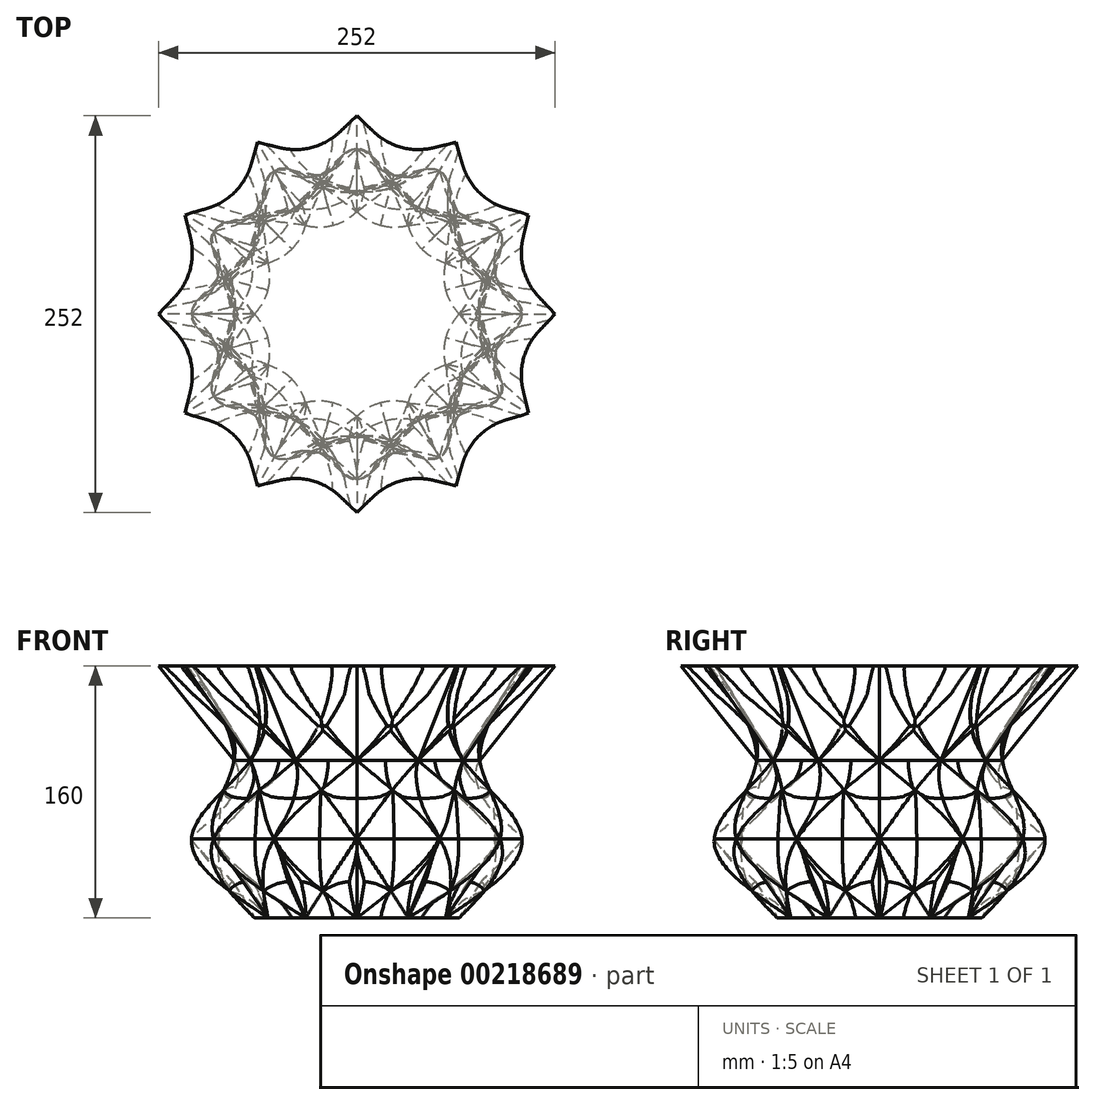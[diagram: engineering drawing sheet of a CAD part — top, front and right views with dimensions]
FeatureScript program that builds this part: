
annotation { "Feature Type Name" : "Feature", "Feature Type Description" : "" }
export const myFeature = defineFeature(function(context is Context, id is Id, definition is map)
    precondition{}
    {
        {
            var Q0;
            Q0=qCreatedBy(makeId("Top.planeOp"),FACE);
            var sketch = newSketch(context, id + "F0", { "sketchPlane" : qUnion([Q0])});
            skCircle(sketch, "E0", {"center": v(0, 0) * mm, "radius": 53.63 * mm, "construction": true});
            skLineSegment(sketch, "E1", {"start": v(-13.88, 51.8) * mm, "end": v(0, 65.07) * mm});
            skLineSegment(sketch, "E2.MirrorCS", {"start": v(13.88, 51.8) * mm, "end": v(0, 65.07) * mm});
            skLineSegment(sketch, "E3.1.0", {"start": v(-37.93, 37.93) * mm, "end": v(-32.54, 56.35) * mm});
            skLineSegment(sketch, "E3.1.1", {"start": v(-13.88, 51.8) * mm, "end": v(-32.54, 56.35) * mm});
            skLineSegment(sketch, "E3.2.0", {"start": v(-51.8, 13.88) * mm, "end": v(-56.35, 32.54) * mm});
            skLineSegment(sketch, "E3.2.1", {"start": v(-37.93, 37.93) * mm, "end": v(-56.35, 32.54) * mm});
            skLineSegment(sketch, "E3.3.0", {"start": v(-51.8, -13.88) * mm, "end": v(-65.07, 0) * mm});
            skLineSegment(sketch, "E3.3.1", {"start": v(-51.8, 13.88) * mm, "end": v(-65.07, 0) * mm});
            skLineSegment(sketch, "E3.4.0", {"start": v(-37.93, -37.93) * mm, "end": v(-56.35, -32.54) * mm});
            skLineSegment(sketch, "E3.4.1", {"start": v(-51.8, -13.88) * mm, "end": v(-56.35, -32.54) * mm});
            skLineSegment(sketch, "E3.5.0", {"start": v(-13.88, -51.8) * mm, "end": v(-32.54, -56.35) * mm});
            skLineSegment(sketch, "E3.5.1", {"start": v(-37.93, -37.93) * mm, "end": v(-32.54, -56.35) * mm});
            skLineSegment(sketch, "E3.6.0", {"start": v(13.88, -51.8) * mm, "end": v(0, -65.07) * mm});
            skLineSegment(sketch, "E3.6.1", {"start": v(-13.88, -51.8) * mm, "end": v(0, -65.07) * mm});
            skLineSegment(sketch, "E3.7.0", {"start": v(37.93, -37.93) * mm, "end": v(32.54, -56.35) * mm});
            skLineSegment(sketch, "E3.7.1", {"start": v(13.88, -51.8) * mm, "end": v(32.54, -56.35) * mm});
            skLineSegment(sketch, "E3.8.0", {"start": v(51.8, -13.88) * mm, "end": v(56.35, -32.54) * mm});
            skLineSegment(sketch, "E3.8.1", {"start": v(37.93, -37.93) * mm, "end": v(56.35, -32.54) * mm});
            skLineSegment(sketch, "E3.9.0", {"start": v(51.8, 13.88) * mm, "end": v(65.07, 0) * mm});
            skLineSegment(sketch, "E3.9.1", {"start": v(51.8, -13.88) * mm, "end": v(65.07, 0) * mm});
            skLineSegment(sketch, "E3.10.0", {"start": v(37.93, 37.93) * mm, "end": v(56.35, 32.54) * mm});
            skLineSegment(sketch, "E3.10.1", {"start": v(51.8, 13.88) * mm, "end": v(56.35, 32.54) * mm});
            skLineSegment(sketch, "E3.11.0", {"start": v(13.88, 51.8) * mm, "end": v(32.54, 56.35) * mm});
            skLineSegment(sketch, "E3.11.1", {"start": v(37.93, 37.93) * mm, "end": v(32.54, 56.35) * mm});
            skSolve(sketch);
        }
        {
            var Q0;
            Q0 = qSketchRegion(id + "F0", true);
            extrude(context, id + "F1", {"entities" : qUnion([Q0]), "depth" : 50 * mm, "hasDraft" : true, "draftAngle" : 30 * degree});
        }
        {
            var Q0;
            Q0=makeQuery(id+"F1.opExtrude","SWEPT_EDGE",EDGE,{"disambiguationData":[OSD([sQuery(id+"F0.wireOp",EDGE,"E3.1.0"),sQuery(id+"F0.wireOp",EDGE,"E3.2.1")])]});
            var Q1;
            Q1=makeQuery(id+"F1.opExtrude","SWEPT_EDGE",EDGE,{"disambiguationData":[OSD([sQuery(id+"F0.wireOp",EDGE,"E3.2.0"),sQuery(id+"F0.wireOp",EDGE,"E3.3.1")])]});
            var Q2;
            Q2=makeQuery(id+"F1.opExtrude","SWEPT_EDGE",EDGE,{"disambiguationData":[OSD([sQuery(id+"F0.wireOp",EDGE,"E3.3.0"),sQuery(id+"F0.wireOp",EDGE,"E3.4.1")])]});
            var Q3;
            Q3=makeQuery(id+"F1.opExtrude","SWEPT_EDGE",EDGE,{"disambiguationData":[OSD([sQuery(id+"F0.wireOp",EDGE,"E3.4.0"),sQuery(id+"F0.wireOp",EDGE,"E3.5.1")])]});
            var Q4;
            Q4=makeQuery(id+"F1.opExtrude","SWEPT_EDGE",EDGE,{"disambiguationData":[OSD([sQuery(id+"F0.wireOp",EDGE,"E3.5.0"),sQuery(id+"F0.wireOp",EDGE,"E3.6.1")])]});
            var Q5;
            Q5=makeQuery(id+"F1.opExtrude","SWEPT_EDGE",EDGE,{"disambiguationData":[OSD([sQuery(id+"F0.wireOp",EDGE,"E3.6.0"),sQuery(id+"F0.wireOp",EDGE,"E3.7.1")])]});
            var Q6;
            Q6=makeQuery(id+"F1.opExtrude","SWEPT_EDGE",EDGE,{"disambiguationData":[OSD([sQuery(id+"F0.wireOp",EDGE,"E3.7.0"),sQuery(id+"F0.wireOp",EDGE,"E3.8.1")])]});
            var Q7;
            Q7=makeQuery(id+"F1.opExtrude","SWEPT_EDGE",EDGE,{"disambiguationData":[OSD([sQuery(id+"F0.wireOp",EDGE,"E3.8.0"),sQuery(id+"F0.wireOp",EDGE,"E3.9.1")])]});
            var Q8;
            Q8=makeQuery(id+"F1.opExtrude","SWEPT_EDGE",EDGE,{"disambiguationData":[OSD([sQuery(id+"F0.wireOp",EDGE,"E3.9.0"),sQuery(id+"F0.wireOp",EDGE,"E3.10.1")])]});
            var Q9;
            Q9=makeQuery(id+"F1.opExtrude","SWEPT_EDGE",EDGE,{"disambiguationData":[OSD([sQuery(id+"F0.wireOp",EDGE,"E3.10.0"),sQuery(id+"F0.wireOp",EDGE,"E3.11.1")])]});
            var Q10;
            Q10=makeQuery(id+"F1.opExtrude","SWEPT_EDGE",EDGE,{"disambiguationData":[OSD([sQuery(id+"F0.wireOp",EDGE,"E2.MirrorCS"),sQuery(id+"F0.wireOp",EDGE,"E3.11.0")])]});
            var Q11;
            Q11=makeQuery(id+"F1.opExtrude","SWEPT_EDGE",EDGE,{"disambiguationData":[OSD([sQuery(id+"F0.wireOp",EDGE,"E1"),sQuery(id+"F0.wireOp",EDGE,"E3.1.1")])]});
            fillet(context, id + "F2", {"entities" : qUnion([Q0, Q1, Q2, Q3, Q4, Q5, Q6, Q7, Q8, Q9, Q10, Q11]), "radius" : 40 * mm, "tangentPropagation" : true, "allowEdgeOverflow" : false});
        }
        {
            var Q0;
            Q0=makeQuery(id+"F1.opExtrude","SWEPT_BODY",BODY,{"disambiguationData":[OSD([sQuery(id+"F0.wireOp",EDGE,"E1"),sQuery(id+"F0.wireOp",EDGE,"E2.MirrorCS"),sQuery(id+"F0.wireOp",EDGE,"E3.1.0"),sQuery(id+"F0.wireOp",EDGE,"E3.1.1"),sQuery(id+"F0.wireOp",EDGE,"E3.2.0"),sQuery(id+"F0.wireOp",EDGE,"E3.2.1"),sQuery(id+"F0.wireOp",EDGE,"E3.3.0"),sQuery(id+"F0.wireOp",EDGE,"E3.3.1"),sQuery(id+"F0.wireOp",EDGE,"E3.4.0"),sQuery(id+"F0.wireOp",EDGE,"E3.4.1"),sQuery(id+"F0.wireOp",EDGE,"E3.5.0"),sQuery(id+"F0.wireOp",EDGE,"E3.5.1"),sQuery(id+"F0.wireOp",EDGE,"E3.6.0"),sQuery(id+"F0.wireOp",EDGE,"E3.6.1"),sQuery(id+"F0.wireOp",EDGE,"E3.7.0"),sQuery(id+"F0.wireOp",EDGE,"E3.7.1"),sQuery(id+"F0.wireOp",EDGE,"E3.8.0"),sQuery(id+"F0.wireOp",EDGE,"E3.8.1"),sQuery(id+"F0.wireOp",EDGE,"E3.9.0"),sQuery(id+"F0.wireOp",EDGE,"E3.9.1"),sQuery(id+"F0.wireOp",EDGE,"E3.10.0"),sQuery(id+"F0.wireOp",EDGE,"E3.10.1"),sQuery(id+"F0.wireOp",EDGE,"E3.11.0"),sQuery(id+"F0.wireOp",EDGE,"E3.11.1")])]});
            var Q1;
            Q1=qCreatedBy(makeId("Origin.pointOp"),VERTEX);
            transform(context, id + "F3", {"entities" : qUnion([Q0]), "transformType" : TransformType.SCALE_UNIFORMLY, "scale" : 1.2, "scalePoint" : qUnion([Q1]), "makeCopy" : true});
        }
        {
            var Q0;
            Q0=makeQuery(id+"F3.opPattern","COPY",BODY,{"derivedFrom":makeQuery(id+"F1.opExtrude","SWEPT_BODY",BODY,{"disambiguationData":[OSD([sQuery(id+"F0.wireOp",EDGE,"E1"),sQuery(id+"F0.wireOp",EDGE,"E2.MirrorCS"),sQuery(id+"F0.wireOp",EDGE,"E3.1.0"),sQuery(id+"F0.wireOp",EDGE,"E3.1.1"),sQuery(id+"F0.wireOp",EDGE,"E3.2.0"),sQuery(id+"F0.wireOp",EDGE,"E3.2.1"),sQuery(id+"F0.wireOp",EDGE,"E3.3.0"),sQuery(id+"F0.wireOp",EDGE,"E3.3.1"),sQuery(id+"F0.wireOp",EDGE,"E3.4.0"),sQuery(id+"F0.wireOp",EDGE,"E3.4.1"),sQuery(id+"F0.wireOp",EDGE,"E3.5.0"),sQuery(id+"F0.wireOp",EDGE,"E3.5.1"),sQuery(id+"F0.wireOp",EDGE,"E3.6.0"),sQuery(id+"F0.wireOp",EDGE,"E3.6.1"),sQuery(id+"F0.wireOp",EDGE,"E3.7.0"),sQuery(id+"F0.wireOp",EDGE,"E3.7.1"),sQuery(id+"F0.wireOp",EDGE,"E3.8.0"),sQuery(id+"F0.wireOp",EDGE,"E3.8.1"),sQuery(id+"F0.wireOp",EDGE,"E3.9.0"),sQuery(id+"F0.wireOp",EDGE,"E3.9.1"),sQuery(id+"F0.wireOp",EDGE,"E3.10.0"),sQuery(id+"F0.wireOp",EDGE,"E3.10.1"),sQuery(id+"F0.wireOp",EDGE,"E3.11.0"),sQuery(id+"F0.wireOp",EDGE,"E3.11.1")])]}),"instanceName":"1"});
            transform(context, id + "F4", {"entities" : qUnion([Q0]), "transformType" : TransformType.TRANSLATION_3D, "dx" : 0 * mm, "dy" : 0 * mm, "dz" : 100 * mm, "makeCopy" : false});
        }
        {
            var Q1;
            Q1=makeQuery(id+"F1.opExtrude","CAP_FACE",FACE,{"disambiguationData":[OSD([sQuery(id+"F0.wireOp",EDGE,"E1"),sQuery(id+"F0.wireOp",EDGE,"E2.MirrorCS"),sQuery(id+"F0.wireOp",EDGE,"E3.1.0"),sQuery(id+"F0.wireOp",EDGE,"E3.1.1"),sQuery(id+"F0.wireOp",EDGE,"E3.2.0"),sQuery(id+"F0.wireOp",EDGE,"E3.2.1"),sQuery(id+"F0.wireOp",EDGE,"E3.3.0"),sQuery(id+"F0.wireOp",EDGE,"E3.3.1"),sQuery(id+"F0.wireOp",EDGE,"E3.4.0"),sQuery(id+"F0.wireOp",EDGE,"E3.4.1"),sQuery(id+"F0.wireOp",EDGE,"E3.5.0"),sQuery(id+"F0.wireOp",EDGE,"E3.5.1"),sQuery(id+"F0.wireOp",EDGE,"E3.6.0"),sQuery(id+"F0.wireOp",EDGE,"E3.6.1"),sQuery(id+"F0.wireOp",EDGE,"E3.7.0"),sQuery(id+"F0.wireOp",EDGE,"E3.7.1"),sQuery(id+"F0.wireOp",EDGE,"E3.8.0"),sQuery(id+"F0.wireOp",EDGE,"E3.8.1"),sQuery(id+"F0.wireOp",EDGE,"E3.9.0"),sQuery(id+"F0.wireOp",EDGE,"E3.9.1"),sQuery(id+"F0.wireOp",EDGE,"E3.10.0"),sQuery(id+"F0.wireOp",EDGE,"E3.10.1"),sQuery(id+"F0.wireOp",EDGE,"E3.11.0"),sQuery(id+"F0.wireOp",EDGE,"E3.11.1")])],"isStart":true});
            var Q2;
            Q2=makeQuery(id+"F1.opExtrude","CAP_FACE",FACE,{"disambiguationData":[OSD([sQuery(id+"F0.wireOp",EDGE,"E1"),sQuery(id+"F0.wireOp",EDGE,"E2.MirrorCS"),sQuery(id+"F0.wireOp",EDGE,"E3.1.0"),sQuery(id+"F0.wireOp",EDGE,"E3.1.1"),sQuery(id+"F0.wireOp",EDGE,"E3.2.0"),sQuery(id+"F0.wireOp",EDGE,"E3.2.1"),sQuery(id+"F0.wireOp",EDGE,"E3.3.0"),sQuery(id+"F0.wireOp",EDGE,"E3.3.1"),sQuery(id+"F0.wireOp",EDGE,"E3.4.0"),sQuery(id+"F0.wireOp",EDGE,"E3.4.1"),sQuery(id+"F0.wireOp",EDGE,"E3.5.0"),sQuery(id+"F0.wireOp",EDGE,"E3.5.1"),sQuery(id+"F0.wireOp",EDGE,"E3.6.0"),sQuery(id+"F0.wireOp",EDGE,"E3.6.1"),sQuery(id+"F0.wireOp",EDGE,"E3.7.0"),sQuery(id+"F0.wireOp",EDGE,"E3.7.1"),sQuery(id+"F0.wireOp",EDGE,"E3.8.0"),sQuery(id+"F0.wireOp",EDGE,"E3.8.1"),sQuery(id+"F0.wireOp",EDGE,"E3.9.0"),sQuery(id+"F0.wireOp",EDGE,"E3.9.1"),sQuery(id+"F0.wireOp",EDGE,"E3.10.0"),sQuery(id+"F0.wireOp",EDGE,"E3.10.1"),sQuery(id+"F0.wireOp",EDGE,"E3.11.0"),sQuery(id+"F0.wireOp",EDGE,"E3.11.1")])],"isStart":false});
            var Q3;
            Q3=makeQuery(id+"F3.opPattern","COPY",FACE,{"derivedFrom":makeQuery(id+"F1.opExtrude","CAP_FACE",FACE,{"disambiguationData":[OSD([sQuery(id+"F0.wireOp",EDGE,"E1"),sQuery(id+"F0.wireOp",EDGE,"E2.MirrorCS"),sQuery(id+"F0.wireOp",EDGE,"E3.1.0"),sQuery(id+"F0.wireOp",EDGE,"E3.1.1"),sQuery(id+"F0.wireOp",EDGE,"E3.2.0"),sQuery(id+"F0.wireOp",EDGE,"E3.2.1"),sQuery(id+"F0.wireOp",EDGE,"E3.3.0"),sQuery(id+"F0.wireOp",EDGE,"E3.3.1"),sQuery(id+"F0.wireOp",EDGE,"E3.4.0"),sQuery(id+"F0.wireOp",EDGE,"E3.4.1"),sQuery(id+"F0.wireOp",EDGE,"E3.5.0"),sQuery(id+"F0.wireOp",EDGE,"E3.5.1"),sQuery(id+"F0.wireOp",EDGE,"E3.6.0"),sQuery(id+"F0.wireOp",EDGE,"E3.6.1"),sQuery(id+"F0.wireOp",EDGE,"E3.7.0"),sQuery(id+"F0.wireOp",EDGE,"E3.7.1"),sQuery(id+"F0.wireOp",EDGE,"E3.8.0"),sQuery(id+"F0.wireOp",EDGE,"E3.8.1"),sQuery(id+"F0.wireOp",EDGE,"E3.9.0"),sQuery(id+"F0.wireOp",EDGE,"E3.9.1"),sQuery(id+"F0.wireOp",EDGE,"E3.10.0"),sQuery(id+"F0.wireOp",EDGE,"E3.10.1"),sQuery(id+"F0.wireOp",EDGE,"E3.11.0"),sQuery(id+"F0.wireOp",EDGE,"E3.11.1")])],"isStart":true}),"instanceName":"1"});
            var Q4;
            Q4=makeQuery(id+"F3.opPattern","COPY",FACE,{"derivedFrom":makeQuery(id+"F1.opExtrude","CAP_FACE",FACE,{"disambiguationData":[OSD([sQuery(id+"F0.wireOp",EDGE,"E1"),sQuery(id+"F0.wireOp",EDGE,"E2.MirrorCS"),sQuery(id+"F0.wireOp",EDGE,"E3.1.0"),sQuery(id+"F0.wireOp",EDGE,"E3.1.1"),sQuery(id+"F0.wireOp",EDGE,"E3.2.0"),sQuery(id+"F0.wireOp",EDGE,"E3.2.1"),sQuery(id+"F0.wireOp",EDGE,"E3.3.0"),sQuery(id+"F0.wireOp",EDGE,"E3.3.1"),sQuery(id+"F0.wireOp",EDGE,"E3.4.0"),sQuery(id+"F0.wireOp",EDGE,"E3.4.1"),sQuery(id+"F0.wireOp",EDGE,"E3.5.0"),sQuery(id+"F0.wireOp",EDGE,"E3.5.1"),sQuery(id+"F0.wireOp",EDGE,"E3.6.0"),sQuery(id+"F0.wireOp",EDGE,"E3.6.1"),sQuery(id+"F0.wireOp",EDGE,"E3.7.0"),sQuery(id+"F0.wireOp",EDGE,"E3.7.1"),sQuery(id+"F0.wireOp",EDGE,"E3.8.0"),sQuery(id+"F0.wireOp",EDGE,"E3.8.1"),sQuery(id+"F0.wireOp",EDGE,"E3.9.0"),sQuery(id+"F0.wireOp",EDGE,"E3.9.1"),sQuery(id+"F0.wireOp",EDGE,"E3.10.0"),sQuery(id+"F0.wireOp",EDGE,"E3.10.1"),sQuery(id+"F0.wireOp",EDGE,"E3.11.0"),sQuery(id+"F0.wireOp",EDGE,"E3.11.1")])],"isStart":false}),"instanceName":"1"});
            var Q5;
            Q5=makeQuery(id+"F1.opExtrude","CAP_VERTEX",VERTEX,{"disambiguationData":[OSD([sQuery(id+"F0.wireOp",EDGE,"E1"),sQuery(id+"F0.wireOp",EDGE,"E2.MirrorCS")])],"isStart":true});
            var Q6;
            Q6=makeQuery(id+"F1.opExtrude","CAP_VERTEX",VERTEX,{"disambiguationData":[OSD([sQuery(id+"F0.wireOp",EDGE,"E3.11.0"),sQuery(id+"F0.wireOp",EDGE,"E3.11.1")])],"isStart":false});
            var Q7;
            Q7=makeQuery(id+"F3.opPattern","COPY",VERTEX,{"derivedFrom":makeQuery(id+"F1.opExtrude","CAP_VERTEX",VERTEX,{"disambiguationData":[OSD([sQuery(id+"F0.wireOp",EDGE,"E3.10.0"),sQuery(id+"F0.wireOp",EDGE,"E3.10.1")])],"isStart":true}),"instanceName":"1"});
            var Q8;
            Q8=makeQuery(id+"F3.opPattern","COPY",VERTEX,{"derivedFrom":makeQuery(id+"F1.opExtrude","CAP_VERTEX",VERTEX,{"disambiguationData":[OSD([sQuery(id+"F0.wireOp",EDGE,"E3.9.0"),sQuery(id+"F0.wireOp",EDGE,"E3.9.1")])],"isStart":false}),"instanceName":"1"});
            loft(context, id + "F5", {"sheetProfilesArray" : [{ "sheetProfileEntities" : qUnion([Q1]) }, { "sheetProfileEntities" : qUnion([Q2]) }, { "sheetProfileEntities" : qUnion([Q3]) }, { "sheetProfileEntities" : qUnion([Q4]) }], "matchConnections" : true, "connections" : [{ "connectionEntities" : qUnion([Q5, Q6, Q7, Q8]), "connectionEdgeQueries" : qUnion([]), "connectionEdgeParameters" : [] }]});
        }
        {
            var Q0;
            Q0=makeQuery(id+"F5.opLoft","SWEPT_BODY",BODY,{"disambiguationData":[OSD([sQuery(id+"F0.wireOp",EDGE,"E1"),sQuery(id+"F0.wireOp",EDGE,"E2.MirrorCS"),sQuery(id+"F0.wireOp",EDGE,"E3.1.0"),sQuery(id+"F0.wireOp",EDGE,"E3.1.1"),sQuery(id+"F0.wireOp",EDGE,"E3.2.0"),sQuery(id+"F0.wireOp",EDGE,"E3.2.1"),sQuery(id+"F0.wireOp",EDGE,"E3.3.0"),sQuery(id+"F0.wireOp",EDGE,"E3.3.1"),sQuery(id+"F0.wireOp",EDGE,"E3.4.0"),sQuery(id+"F0.wireOp",EDGE,"E3.4.1"),sQuery(id+"F0.wireOp",EDGE,"E3.5.0"),sQuery(id+"F0.wireOp",EDGE,"E3.5.1"),sQuery(id+"F0.wireOp",EDGE,"E3.6.0"),sQuery(id+"F0.wireOp",EDGE,"E3.6.1"),sQuery(id+"F0.wireOp",EDGE,"E3.7.0"),sQuery(id+"F0.wireOp",EDGE,"E3.7.1"),sQuery(id+"F0.wireOp",EDGE,"E3.8.0"),sQuery(id+"F0.wireOp",EDGE,"E3.8.1"),sQuery(id+"F0.wireOp",EDGE,"E3.9.0"),sQuery(id+"F0.wireOp",EDGE,"E3.9.1"),sQuery(id+"F0.wireOp",EDGE,"E3.10.0"),sQuery(id+"F0.wireOp",EDGE,"E3.10.1"),sQuery(id+"F0.wireOp",EDGE,"E3.11.0"),sQuery(id+"F0.wireOp",EDGE,"E3.11.1")])]});
            var Q1;
            Q1=qCreatedBy(makeId("Front.planeOp"),FACE);
            mirror(context, id + "F6", {"operationType" : NewBodyOperationType.ADD, "entities" : qUnion([Q0]), "mirrorPlane" : qUnion([Q1])});
        }
    });
